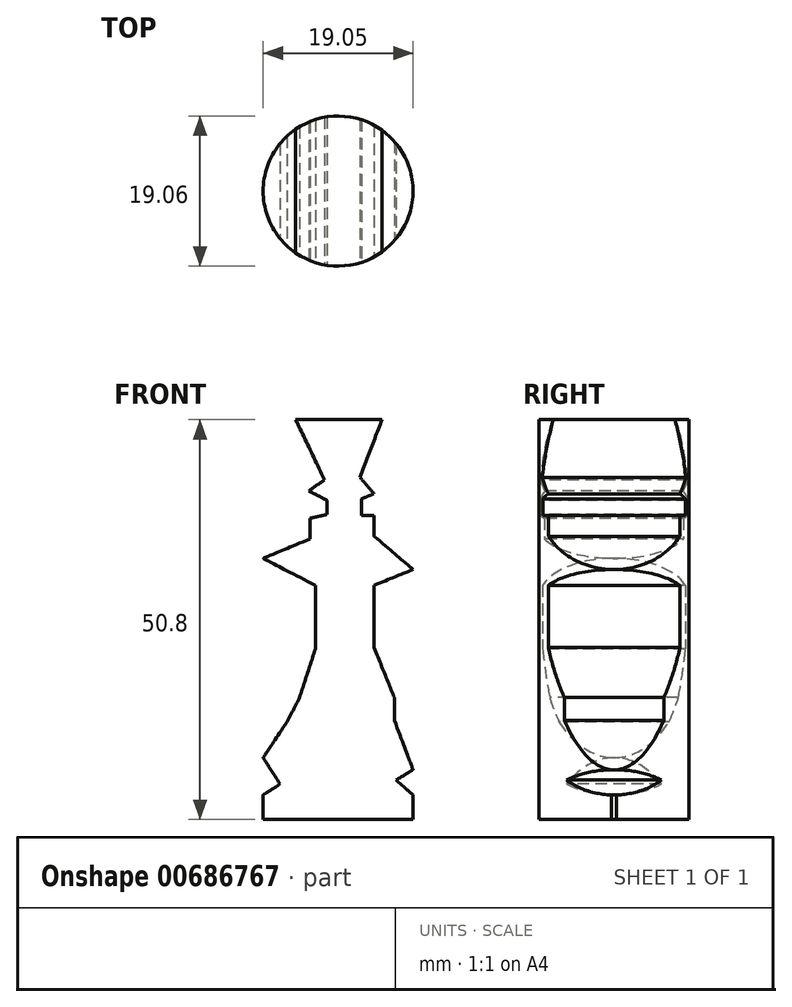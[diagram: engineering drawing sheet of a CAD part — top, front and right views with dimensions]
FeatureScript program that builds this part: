
annotation { "Feature Type Name" : "Feature", "Feature Type Description" : "" }
export const myFeature = defineFeature(function(context is Context, id is Id, definition is map)
    precondition{}
    {
        {
            var Q0;
            Q0=qCreatedBy(makeId("Top.planeOp"),FACE);
            var sketch = newSketch(context, id + "F0", { "sketchPlane" : qUnion([Q0])});
            skCircle(sketch, "E0", {"center": v(9.53, 0) * mm, "radius": 9.53 * mm});
            skSolve(sketch);
        }
        {
            var Q0;
            Q0 = qSketchRegion(id + "F0", true);
            extrude(context, id + "F1", {"entities" : qUnion([Q0]), "depth" : 50.8 * mm, "offsetDistance" : 25.4 * mm});
        }
        {
            var Q0;
            Q0=qCreatedBy(makeId("Front.planeOp"),FACE);
            var sketch = newSketch(context, id + "F2", { "sketchPlane" : qUnion([Q0])});
            skLineSegment(sketch, "E1", {"start": v(0, 0) * mm, "end": v(0, 3.12) * mm});
            skLineSegment(sketch, "E2", {"start": v(19.05, 3.12) * mm, "end": v(19.05, 0) * mm});
            skLineSegment(sketch, "E3", {"start": v(19.05, 3.12) * mm, "end": v(16.89, 5) * mm});
            skLineSegment(sketch, "E4", {"start": v(16.89, 5) * mm, "end": v(19.05, 6.32) * mm});
            skLineSegment(sketch, "E5", {"start": v(19.05, 6.32) * mm, "end": v(16.67, 12.6) * mm});
            skLineSegment(sketch, "E6", {"start": v(16.67, 12.6) * mm, "end": v(16.67, 15.48) * mm});
            skLineSegment(sketch, "E7", {"start": v(16.67, 15.48) * mm, "end": v(14.1, 21.85) * mm});
            skLineSegment(sketch, "E8", {"start": v(14.1, 21.85) * mm, "end": v(14.1, 29.75) * mm});
            skLineSegment(sketch, "E9", {"start": v(14.1, 29.75) * mm, "end": v(19.05, 31.75) * mm});
            skLineSegment(sketch, "E10", {"start": v(19.05, 31.75) * mm, "end": v(14.1, 35.98) * mm});
            skLineSegment(sketch, "E11", {"start": v(14.1, 35.98) * mm, "end": v(14.1, 38.62) * mm});
            skLineSegment(sketch, "E12", {"start": v(14.1, 38.62) * mm, "end": v(12.5, 38.62) * mm});
            skLineSegment(sketch, "E13", {"start": v(12.5, 38.62) * mm, "end": v(12.5, 40.73) * mm});
            skLineSegment(sketch, "E14", {"start": v(12.5, 40.73) * mm, "end": v(14.1, 41.38) * mm});
            skLineSegment(sketch, "E15", {"start": v(14.1, 41.38) * mm, "end": v(12.28, 43.48) * mm});
            skLineSegment(sketch, "E16", {"start": v(12.28, 43.48) * mm, "end": v(15.13, 50.86) * mm});
            skLineSegment(sketch, "E17", {"start": v(15.13, 50.86) * mm, "end": v(19.05, 50.86) * mm});
            skLineSegment(sketch, "E18", {"start": v(19.05, 50.86) * mm, "end": v(22.94, 50.86) * mm});
            skLineSegment(sketch, "E19", {"start": v(22.94, 50.86) * mm, "end": v(22.1, 0) * mm});
            skLineSegment(sketch, "E20", {"start": v(22.1, 0) * mm, "end": v(19.05, 0) * mm});
            skLineSegment(sketch, "E21", {"start": v(0, 3.12) * mm, "end": v(2.15, 4.5) * mm});
            skLineSegment(sketch, "E22", {"start": v(2.15, 4.5) * mm, "end": v(0, 7.85) * mm});
            skLineSegment(sketch, "E23", {"start": v(0, 7.85) * mm, "end": v(3.04, 12.4) * mm});
            skLineSegment(sketch, "E24", {"start": v(3.04, 12.4) * mm, "end": v(4.63, 15.48) * mm});
            skLineSegment(sketch, "E25", {"start": v(4.63, 15.48) * mm, "end": v(6.63, 21.67) * mm});
            skLineSegment(sketch, "E26", {"start": v(6.63, 21.67) * mm, "end": v(6.63, 29.75) * mm});
            skLineSegment(sketch, "E27", {"start": v(6.63, 29.75) * mm, "end": v(0, 33.17) * mm});
            skLineSegment(sketch, "E28", {"start": v(0, 33.17) * mm, "end": v(5.96, 35.65) * mm});
            skLineSegment(sketch, "E29", {"start": v(5.96, 35.65) * mm, "end": v(5.96, 38.27) * mm});
            skLineSegment(sketch, "E30", {"start": v(5.96, 38.27) * mm, "end": v(8.14, 38.75) * mm});
            skLineSegment(sketch, "E31", {"start": v(8.14, 38.75) * mm, "end": v(8.14, 40.53) * mm});
            skLineSegment(sketch, "E32", {"start": v(8.14, 40.53) * mm, "end": v(5.81, 41.73) * mm});
            skLineSegment(sketch, "E33", {"start": v(5.81, 41.73) * mm, "end": v(7.78, 43.15) * mm});
            skLineSegment(sketch, "E34", {"start": v(7.78, 43.15) * mm, "end": v(4.1, 50.86) * mm});
            skLineSegment(sketch, "E35", {"start": v(4.1, 50.86) * mm, "end": v(-2.77, 50.86) * mm});
            skLineSegment(sketch, "E36", {"start": v(-2.77, 50.86) * mm, "end": v(-2.77, 0) * mm});
            skLineSegment(sketch, "E37", {"start": v(-2.77, 0) * mm, "end": v(0, 0) * mm});
            skSolve(sketch);
        }
        {
            var Q0;
            Q0 = qSketchRegion(id + "F2", true);
            extrude(context, id + "F3", {"entities" : qUnion([Q0]), "operationType" : NewBodyOperationType.REMOVE, "endBound" : BoundingType.SYMMETRIC, "oppositeDirection" : true, "depth" : 25.4 * mm, "offsetDistance" : 25.4 * mm});
        }
    });
